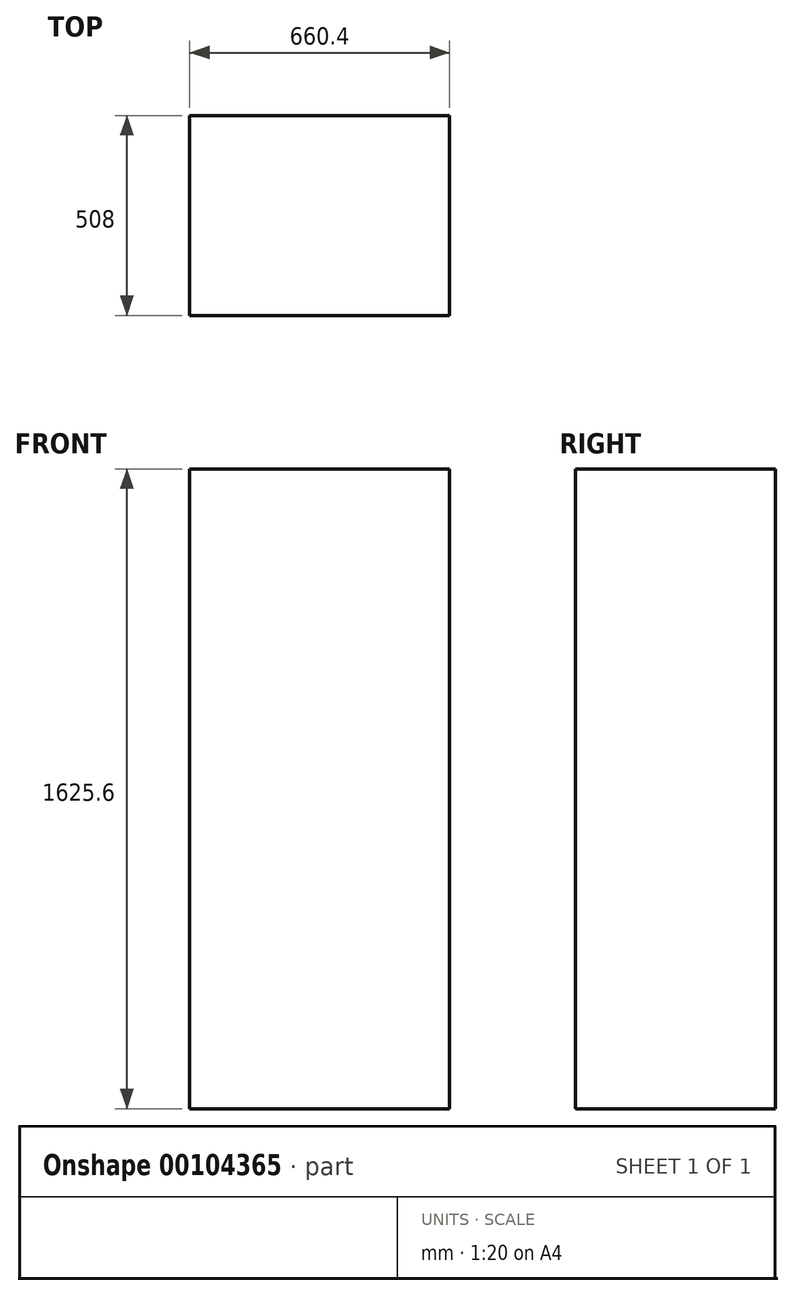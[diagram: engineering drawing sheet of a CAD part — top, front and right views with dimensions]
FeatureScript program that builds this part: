
annotation { "Feature Type Name" : "Feature", "Feature Type Description" : "" }
export const myFeature = defineFeature(function(context is Context, id is Id, definition is map)
    precondition{}
    {
        {
            var Q0;
            Q0=qCreatedBy(makeId("Top.planeOp"),FACE);
            var sketch = newSketch(context, id + "F0", { "sketchPlane" : qUnion([Q0])});
            skLineSegment(sketch, "E0.bottom", {"start": v(0, 0) * mm, "end": v(660.4, 0) * mm});
            skLineSegment(sketch, "E0.top", {"start": v(0, 508) * mm, "end": v(660.4, 508) * mm});
            skLineSegment(sketch, "E0.left", {"start": v(0, 0) * mm, "end": v(0, 508) * mm});
            skLineSegment(sketch, "E0.right", {"start": v(660.4, 0) * mm, "end": v(660.4, 508) * mm});
            skSolve(sketch);
        }
        {
            var Q0;
            Q0 = qSketchRegion(id + "F0", true);
            extrude(context, id + "F1", {"entities" : qUnion([Q0]), "depth" : 1625.6 * mm});
        }
    });
